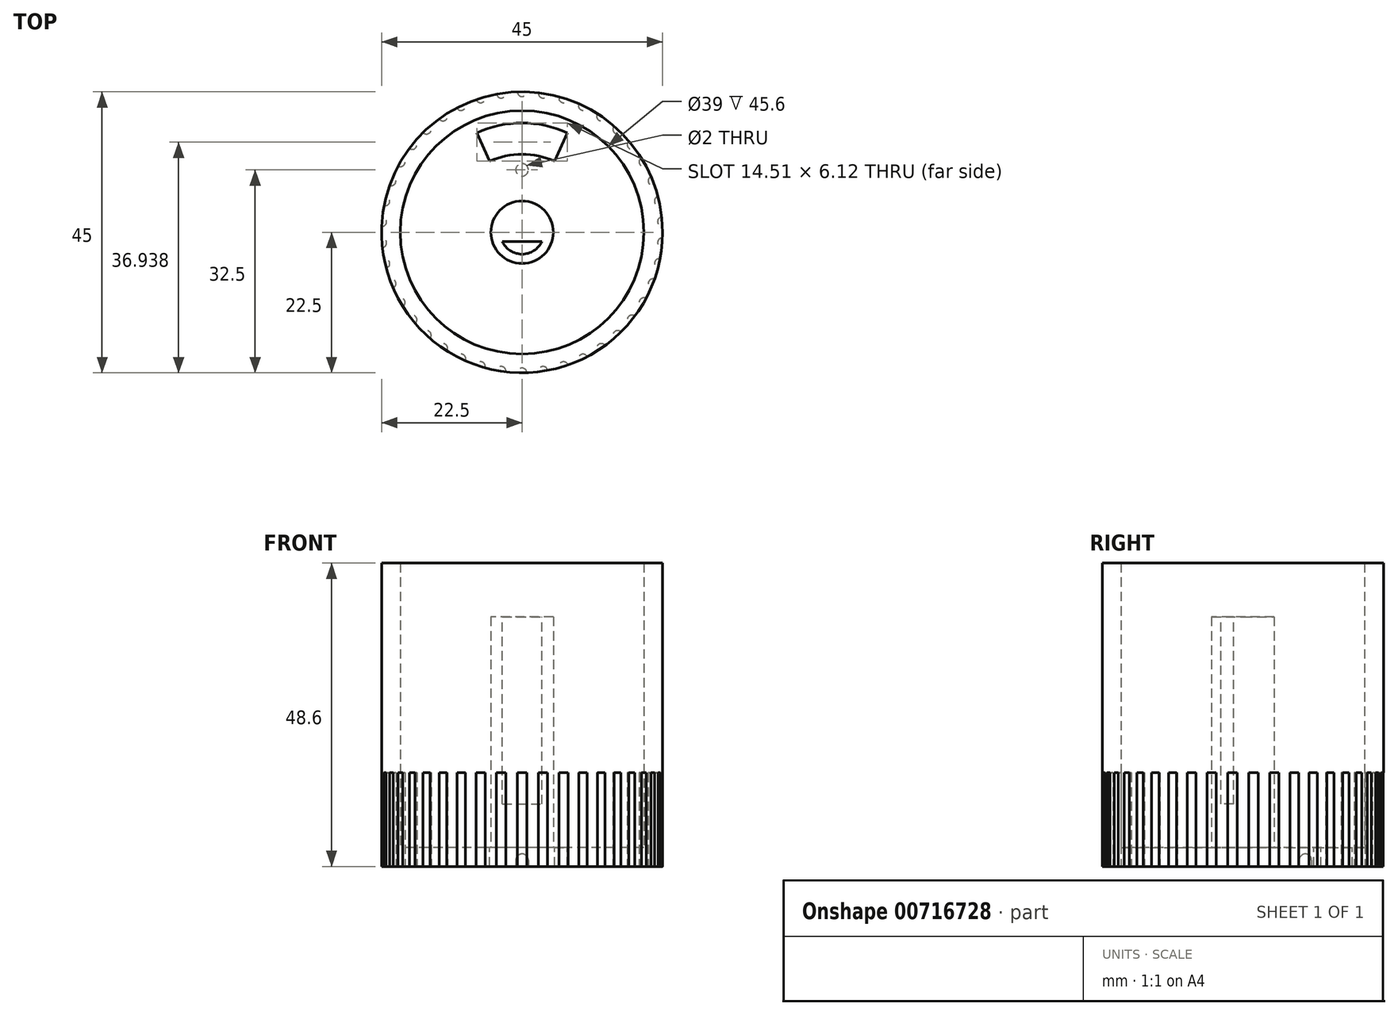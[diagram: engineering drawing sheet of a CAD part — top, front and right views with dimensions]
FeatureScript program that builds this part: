
annotation { "Feature Type Name" : "Feature", "Feature Type Description" : "" }
export const myFeature = defineFeature(function(context is Context, id is Id, definition is map)
    precondition{}
    {
        {
            var Q0;
            Q0=qCreatedBy(makeId("Top.planeOp"),FACE);
            var sketch = newSketch(context, id + "F10", { "sketchPlane" : qUnion([Q0])});
            skCircle(sketch, "E0", {"center": v(0, 0) * mm, "radius": 22.5 * mm});
            skSolve(sketch);
        }
        {
            var Q0;
            Q0=makeQuery(id+"F10.imprint","IMPRINT",FACE,{"disambiguationData":[TD([[makeQuery(id+"F10.imprint","IMPRINT",EDGE,{"derivedFrom":sQuery(id+"F10.wireOp",EDGE,"E0")}),1.0]])]});
            extrude(context, id + "F0", {"entities" : qUnion([Q0]), "depth" : 48.6 * mm});
        }
        {
            var Q0;
            Q0=makeQuery(id+"F0.opExtrude","CAP_FACE",FACE,{"disambiguationData":[OSD([sQuery(id+"F10.wireOp",EDGE,"E0")])],"isStart":false});
            shell(context, id + "F1", {"entities" : qUnion([Q0]), "thickness" : 3 * mm});
        }
        {
            var Q0;
            {var subQ0=sQuery(id+"F10.wireOp",EDGE,"E0");Q0=makeQuery(id+"F1.opShell","OFFSET_FACE",FACE,{"disambiguationData":[OSD([subQ0]),TDD([makeQuery(id+"F0.opExtrude","CAP_FACE",FACE,{"disambiguationData":[OSD([subQ0])],"isStart":true})])]});}
            var sketch = newSketch(context, id + "F2", { "sketchPlane" : qUnion([Q0])});
            skCircle(sketch, "E1", {"center": v(0, 0) * mm, "radius": 5 * mm});
            skSolve(sketch);
        }
        {
            var Q0;
            Q0=qSketchRegion(id+"F2",true);
            extrude(context, id + "F3", {"entities" : qUnion([Q0]), "operationType" : NewBodyOperationType.ADD, "depth" : 37 * mm});
        }
        {
            var Q0;
            Q0=makeQuery(id+"F3.opExtrude","CAP_FACE",FACE,{"disambiguationData":[OSD([sQuery(id+"F2.wireOp",EDGE,"E1")])],"isStart":false});
            var sketch = newSketch(context, id + "F4", { "sketchPlane" : qUnion([Q0])});
            skCircle(sketch, "E2", {"center": v(0, 0) * mm, "radius": 3.5 * mm});
            skPoint(sketch, "E3", {"position": v(0, 3.5) * mm});
            skLineSegment(sketch, "E4", {"start": v(-3.9, -1.5) * mm, "end": v(4, -1.5) * mm});
            skSolve(sketch);
        }
        {
            var Q0;
            {var subQ0=sQuery(id+"F4.wireOp",EDGE,"E4");var subQ1=sQuery(id+"F4.wireOp",EDGE,"E2");var subQ2=makeQuery(id+"F4.imprint","INTERSECT",VERTEX,{"disambiguationData":[OD(0.0)],"derivedFrom":[subQ1,subQ0]});Q0=makeQuery(id+"F4.imprint","IMPRINT",FACE,{"disambiguationData":[TD([[makeQuery(id+"F4.imprint","IMPRINT",EDGE,{"disambiguationData":[TD([[subQ2,1.0]])],"derivedFrom":subQ1}),1.0]])]});}
            extrude(context, id + "F11", {"entities" : qUnion([Q0]), "operationType" : NewBodyOperationType.REMOVE, "oppositeDirection" : true, "depth" : 30 * mm});
        }
        {
            var Q0;
            {var subQ0=sQuery(id+"F10.wireOp",EDGE,"E0");Q0=makeQuery(id+"F1.opShell","OFFSET_FACE",FACE,{"disambiguationData":[OSD([subQ0]),TDD([makeQuery(id+"F0.opExtrude","CAP_FACE",FACE,{"disambiguationData":[OSD([subQ0])],"isStart":true})])]});}
            var sketch = newSketch(context, id + "F12", { "sketchPlane" : qUnion([Q0])});
            skCircle(sketch, "E5", {"center": v(0, 0) * mm, "radius": 17.5 * mm});
            skCircle(sketch, "E6", {"center": v(0, 0) * mm, "radius": 12.5 * mm});
            skLineSegment(sketch, "E7", {"start": v(0, 0) * mm, "end": v(7.26, 15.93) * mm});
            skLineSegment(sketch, "E8", {"start": v(0, 0) * mm, "end": v(-7.26, 15.93) * mm});
            skLineSegment(sketch, "E9", {"start": v(-7.26, 15.93) * mm, "end": v(7.26, 15.93) * mm});
            skSolve(sketch);
        }
        {
            var Q0;
            {var subQ5=sQuery(id+"F12.wireOp",EDGE,"E9");Q0=makeQuery(id+"F12.imprint","IMPRINT",FACE,{"disambiguationData":[TD([[makeQuery(id+"F12.imprint","IMPRINT",EDGE,{"derivedFrom":subQ5}),-1.0]])]});}
            var Q1;
            {var subQ0=sQuery(id+"F12.wireOp",EDGE,"E9");Q1=makeQuery(id+"F12.imprint","IMPRINT",FACE,{"disambiguationData":[TD([[makeQuery(id+"F12.imprint","IMPRINT",EDGE,{"derivedFrom":subQ0}),1.0]])]});}
            extrude(context, id + "F5", {"entities" : qUnion([Q0, Q1]), "operationType" : NewBodyOperationType.REMOVE, "oppositeDirection" : true, "depth" : 25 * mm});
        }
        {
            var Q0;
            Q0=makeQuery(id+"F0.opExtrude","CAP_FACE",FACE,{"disambiguationData":[OSD([sQuery(id+"F10.wireOp",EDGE,"E0")])],"isStart":true});
            var sketch = newSketch(context, id + "F13", { "sketchPlane" : qUnion([Q0])});
            skCircle(sketch, "E10", {"center": v(0, -10) * mm, "radius": 1 * mm});
            skSolve(sketch);
        }
        {
            var Q0;
            Q0=makeQuery(id+"F13.imprint","IMPRINT",FACE,{"disambiguationData":[TD([[makeQuery(id+"F13.imprint","IMPRINT",EDGE,{"derivedFrom":sQuery(id+"F13.wireOp",EDGE,"E10")}),1.0]])]});
            extrude(context, id + "F6", {"entities" : qUnion([Q0]), "operationType" : NewBodyOperationType.REMOVE, "oppositeDirection" : true, "depth" : 2 * mm});
        }
        {
            var Q0;
            Q0=makeQuery(id+"F6.boolean.opBoolean","COPY",EDGE,{"derivedFrom":makeQuery(id+"F6.opExtrude","CAP_EDGE",EDGE,{"disambiguationData":[OSD([sQuery(id+"F13.wireOp",EDGE,"E10")])],"isStart":false})});
            fillet(context, id + "F7", {"entities" : qUnion([Q0]), "radius" : 1 * mm, "tangentPropagation" : true, "allowEdgeOverflow" : false});
        }
        {
            var Q0;
            Q0=makeQuery(id+"F0.opExtrude","CAP_FACE",FACE,{"disambiguationData":[OSD([sQuery(id+"F10.wireOp",EDGE,"E0")])],"isStart":true});
            var sketch = newSketch(context, id + "F8", { "sketchPlane" : qUnion([Q0])});
            skCircle(sketch, "E11", {"center": v(0, -22.5) * mm, "radius": 0.75 * mm});
            skCircle(sketch, "E12.1.0", {"center": v(3.35, -22.25) * mm, "radius": 0.75 * mm});
            skCircle(sketch, "E12.2.0", {"center": v(6.63, -21.5) * mm, "radius": 0.75 * mm});
            skCircle(sketch, "E12.3.0", {"center": v(9.76, -20.27) * mm, "radius": 0.75 * mm});
            skCircle(sketch, "E12.4.0", {"center": v(12.67, -18.6) * mm, "radius": 0.75 * mm});
            skCircle(sketch, "E12.5.0", {"center": v(15.3, -16.5) * mm, "radius": 0.75 * mm});
            skCircle(sketch, "E12.6.0", {"center": v(17.6, -14.03) * mm, "radius": 0.75 * mm});
            skCircle(sketch, "E12.7.0", {"center": v(19.49, -11.25) * mm, "radius": 0.75 * mm});
            skCircle(sketch, "E12.8.0", {"center": v(20.94, -8.22) * mm, "radius": 0.75 * mm});
            skCircle(sketch, "E12.9.0", {"center": v(21.94, -5) * mm, "radius": 0.75 * mm});
            skCircle(sketch, "E12.10.0", {"center": v(22.44, -1.68) * mm, "radius": 0.75 * mm});
            skCircle(sketch, "E12.11.0", {"center": v(22.44, 1.68) * mm, "radius": 0.75 * mm});
            skCircle(sketch, "E12.12.0", {"center": v(21.94, 5) * mm, "radius": 0.75 * mm});
            skCircle(sketch, "E12.13.0", {"center": v(20.94, 8.22) * mm, "radius": 0.75 * mm});
            skCircle(sketch, "E12.14.0", {"center": v(19.49, 11.25) * mm, "radius": 0.75 * mm});
            skCircle(sketch, "E12.15.0", {"center": v(17.6, 14.03) * mm, "radius": 0.75 * mm});
            skCircle(sketch, "E12.16.0", {"center": v(15.3, 16.5) * mm, "radius": 0.75 * mm});
            skCircle(sketch, "E12.17.0", {"center": v(12.67, 18.6) * mm, "radius": 0.75 * mm});
            skCircle(sketch, "E12.18.0", {"center": v(9.76, 20.27) * mm, "radius": 0.75 * mm});
            skCircle(sketch, "E12.19.0", {"center": v(6.63, 21.5) * mm, "radius": 0.75 * mm});
            skCircle(sketch, "E12.20.0", {"center": v(3.35, 22.25) * mm, "radius": 0.75 * mm});
            skCircle(sketch, "E12.21.0", {"center": v(0, 22.5) * mm, "radius": 0.75 * mm});
            skCircle(sketch, "E12.22.0", {"center": v(-3.35, 22.25) * mm, "radius": 0.75 * mm});
            skCircle(sketch, "E12.23.0", {"center": v(-6.63, 21.5) * mm, "radius": 0.75 * mm});
            skCircle(sketch, "E12.24.0", {"center": v(-9.76, 20.27) * mm, "radius": 0.75 * mm});
            skCircle(sketch, "E12.25.0", {"center": v(-12.67, 18.6) * mm, "radius": 0.75 * mm});
            skCircle(sketch, "E12.26.0", {"center": v(-15.3, 16.5) * mm, "radius": 0.75 * mm});
            skCircle(sketch, "E12.27.0", {"center": v(-17.6, 14.03) * mm, "radius": 0.75 * mm});
            skCircle(sketch, "E12.28.0", {"center": v(-19.49, 11.25) * mm, "radius": 0.75 * mm});
            skCircle(sketch, "E12.29.0", {"center": v(-20.94, 8.22) * mm, "radius": 0.75 * mm});
            skCircle(sketch, "E12.30.0", {"center": v(-21.94, 5) * mm, "radius": 0.75 * mm});
            skCircle(sketch, "E12.31.0", {"center": v(-22.44, 1.68) * mm, "radius": 0.75 * mm});
            skCircle(sketch, "E12.32.0", {"center": v(-22.44, -1.68) * mm, "radius": 0.75 * mm});
            skCircle(sketch, "E12.33.0", {"center": v(-21.94, -5) * mm, "radius": 0.75 * mm});
            skCircle(sketch, "E12.34.0", {"center": v(-20.94, -8.22) * mm, "radius": 0.75 * mm});
            skCircle(sketch, "E12.35.0", {"center": v(-19.49, -11.25) * mm, "radius": 0.75 * mm});
            skCircle(sketch, "E12.36.0", {"center": v(-17.6, -14.03) * mm, "radius": 0.75 * mm});
            skCircle(sketch, "E12.37.0", {"center": v(-15.3, -16.5) * mm, "radius": 0.75 * mm});
            skCircle(sketch, "E12.38.0", {"center": v(-12.67, -18.6) * mm, "radius": 0.75 * mm});
            skCircle(sketch, "E12.39.0", {"center": v(-9.76, -20.27) * mm, "radius": 0.75 * mm});
            skCircle(sketch, "E12.40.0", {"center": v(-6.63, -21.5) * mm, "radius": 0.75 * mm});
            skCircle(sketch, "E12.41.0", {"center": v(-3.35, -22.25) * mm, "radius": 0.75 * mm});
            skPoint(sketch, "E12.center", {"position": v(0, 0) * mm});
            skSolve(sketch);
        }
        {
            var Q0;
            Q0=qSketchRegion(id+"F8",true);
            extrude(context, id + "F9", {"entities" : qUnion([Q0]), "operationType" : NewBodyOperationType.REMOVE, "oppositeDirection" : true, "depth" : 15 * mm});
        }
    });
